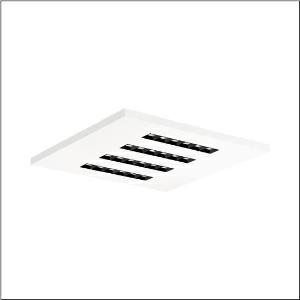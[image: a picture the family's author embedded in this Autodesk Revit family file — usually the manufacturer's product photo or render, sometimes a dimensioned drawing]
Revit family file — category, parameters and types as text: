
# Revit family: silica_r__21_square_51mx6kds44w_0efc
name_source: partatom
category: Lighting Fixtures
units: mm (PartAtom-declared; Revit-internal decimal feet)

## family parameters
Cut with Voids When Loaded = No
Host = Face
Light Source = No
Part Type = Normal
Room Calculation Point = No
Round Connector Dimension = Use Diameter
Shared = No

## types (1)
- --- (1 x LED, 4600 lm, 29.6 W, 4000K)
    Apparent Load = 30 VA
    CIE Flux Codes = 86 100 100 100 100
    Color Rendering = 80
    Color Temperature = 4000K
    Default Elevation = 1800 mm
    Description = Silica® 21 Square, office luminaire, primary light control with lens, of PMMA, primary anti-glare with reflector, of PC, black, CAT 2 (L<= 3000cd/m²), light emission: direct distribution, primary light characteristic: symmetric, installation type: lay-in mounting, LED, rated luminous flux: 4.600lm, luminous efficacy: 155lm/W, light colour: 840, colour temperature: 4000K, with terminal, 5-pole, mains connection: 220..240V, AC, 50/60Hz, rated input power: 29.6W, luminaire housing, of sheet steel, coated, traffic white (RAL 9016), module: M600, length: 597mm, width: 597mm, height: 33mm, protection rating (complete): IP20, insulation class (complete): insulation class I (protective earthing), certification: CE, permissible operating ambient temperature: -20..+40°C, standard: EN 50419, packaging unit: 1 piece
    Height = 0 mm  [stored 0 ft]
    Lamp = 1 x LED
    Lamp Light Flux = 4600 lm
    Lamp Power = 29.6 W
    Lamp count = 1
    Length = 597 mm
    Luminous efficacy = 155 lm/W
    Manufacturer = Siteco
    ModVariant = No
    Model = 51MX6KDS44W
    Mounting Place = Ceiling
    Mounting Type = Recessed
    Number of Poles = 1
    OnlyDefault = Yes
    Power Factor = 1
    Product Name = Silica® 21 Square
    Product group = office luminaire | ceiling recessed
    ProductGroupID = 400
    Protection Class = Protection class I
    Protection Degree = IP 20
    RLX_Detail_Level = 1
    RLX_Emergency_Light_Flux = 0 lm
    RLX_Emergency_Type = 0
    RLX_Emergency_Type_DB = No
    RlxData = <blob elided: 40361 chars, md5=2cdd6147>
    Socket = socket
    Standby Power = 0 W
    System Light Flux = 4600 lm
    System Power = 30 W
    Type Comments = factory setting: luminous flux: 100 % | dim-lin: 254 | 399 mA
    Type Image = l_1275207.jpg
    URL = http://relux.com
    VarID = @adj_053397
    Voltage = 0 V
    Weight = 0.00 kg
    Width = 597 mm

note: [stored X ft] marks values corroborated as IEEE doubles in the binary element streams (Revit-internal decimal feet)

## geometry (parser evidence)
native form markers: Blend x4, Sweep x13
no freeform markers — native parametric forms only
